# Revit family: STS-107 Извещатель охранный_ПРД_RV17_LOD400
name_source: partatom
category: Датчики
revit_build: Autodesk Revit 2017 (Build: 20170118_1100(x64)
units: mm (PartAtom-declared; Revit-internal decimal feet)

## family parameters
Всегда вертикально = Нет
На основе рабочей плоскости = Нет
Общий = Нет
При загрузке вырезать с полостями = Нет
Размер круглого соединителя = Использовать диаметр
Сохранять ориентацию аннотаций = Нет
Тип детали = Нормальный
Точка расчета площади = Нет

## types (1)
- STS-107 Извещатель охранный (Передатчик)
    ADSK_URL страницы изделия = https://stilsoft.ru
    ADSK_Единица измерения = шт.
    ADSK_Завод-изготовитель = ООО «Основа Безопасности»
    ADSK_Количество = 1
    ADSK_Марка = СТВФ.426479.006
    ADSK_Масса = 1.3
    ADSK_Наименование = Извещатель охранный STS-107
    ADSK_Размер_Высота = 141 мм
    ADSK_Размер_Длина = 210 мм
    ADSK_Размер_Ширина = 210 мм
    d_короба = 20 мм
    Вероятность обнаружения, не менее = 0.98
    Время восстановления дежурного режима, не более, с = 10
    Время технической готовности после включения питания, не более, с = 45
    Высота зоны обнаружения на расстоянии, равноудаленном от блоков при максимальной дальности действия, не более, м = 3
    Диапазон рабочих температур, °С = от -50 до +70
    Длина зоны неуверенного обнаружения на расстоянии от передатчика и приемника, не более, м = 2
    Длительность извещения, не менее, с = 2
    Допустимая амплитуда пульсаций напряжения электропитания, не более, В = 0,03*
    Запас по уровню принимаемого сигнала при максимальной длине зоны обнаружения, не менее, дБ = 6
    Интерфейс связи извещателя = RS-485
    Информативность извещателя по шине RS-485 = 19
    Информативность извещателя по шлейфу = 3
    Максимальная высота неровностей земли, снежного и травяного покрова, м = 1
    Напряжение электропитания постоянного тока, В = от 10 до 36
    Наработка на ложное срабатывание не менее, ч = 1200
    Параметры сигнала дистанционного контроля длительность импульса, с, не менее = 0,5
    Параметры сигнала дистанционного контроля напряжение импульса, В = от 5 до 30
    Параметры сигнала, коммутируемого выходными контактами цепей «ТР» и «ТР ДВ» амплитудное напряжение, В, не более = 30
    Параметры сигнала, коммутируемого выходными контактами цепей «ТР» и «ТР ДВ» ток, постоянный или переменный, не более, мА = 120
    Потребляемый ток при рабочем напряжении электропитания 12В передатчика, не более, мА = 160
    Протяженность зоны обнаружения, м = от 5 до 300
    Рабочая частота, ГГц = 24-24,25
    Скорость передвижения нарушителя движущегося в положении «в рост» или «согнувшись», при которой осуществляется обнаружение, м/с = от 0,1 до 10,0
    Среднее время наработки на отказ, не менее, ч = 60000
    Ширина зоны обнаружения на расстоянии, равноудаленном от блоков, при максимальной дальности действия, не более, м = 3
